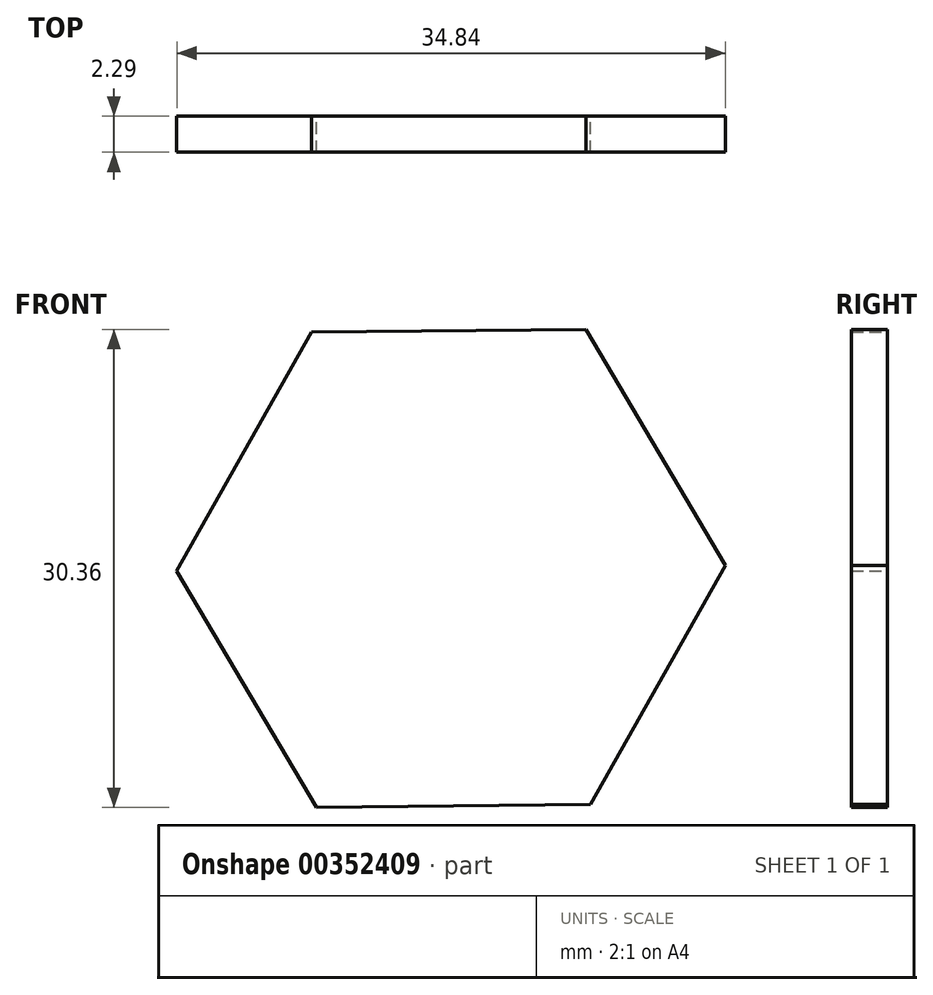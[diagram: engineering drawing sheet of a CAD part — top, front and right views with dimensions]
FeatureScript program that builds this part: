
annotation { "Feature Type Name" : "Feature", "Feature Type Description" : "" }
export const myFeature = defineFeature(function(context is Context, id is Id, definition is map)
    precondition{}
    {
        {
            var Q0;
            Q0=qCreatedBy(makeId("Front.planeOp"),FACE);
            var sketch = newSketch(context, id + "F0", { "sketchPlane" : qUnion([Q0])});
            skCircle(sketch, "E0.cCircle", {"center": v(0, 0) * mm, "radius": 15.09 * mm, "construction": true});
            skLineSegment(sketch, "E0.0", {"start": v(8.56, 15.18) * mm, "end": v(17.42, 0.18) * mm});
            skLineSegment(sketch, "E0.1", {"start": v(17.42, 0.18) * mm, "end": v(8.86, -15) * mm});
            skLineSegment(sketch, "E0.2", {"start": v(8.86, -15) * mm, "end": v(-8.56, -15.18) * mm});
            skLineSegment(sketch, "E0.3", {"start": v(-8.56, -15.18) * mm, "end": v(-17.42, -0.18) * mm});
            skLineSegment(sketch, "E0.4", {"start": v(-17.42, -0.18) * mm, "end": v(-8.86, 15) * mm});
            skLineSegment(sketch, "E0.5", {"start": v(-8.86, 15) * mm, "end": v(8.56, 15.18) * mm});
            skPoint(sketch, "E0.0.midPoint", {"position": v(13, 7.68) * mm});
            skSolve(sketch);
        }
        {
            var Q0;
            Q0=makeQuery(id+"F0.imprint","IMPRINT",FACE,{"disambiguationData":[TD([[makeQuery(id+"F0.imprint","IMPRINT",EDGE,{"derivedFrom":sQuery(id+"F0.wireOp",EDGE,"E0.0")}),-1.0]])]});
            extrude(context, id + "F1", {"entities" : qUnion([Q0]), "depth" : 2.3 * mm});
        }
    });
